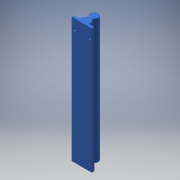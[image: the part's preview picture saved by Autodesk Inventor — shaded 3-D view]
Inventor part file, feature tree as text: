
AUTODESK INVENTOR PART (.ipt)
format: ipt  version: 2018 (Build 220112000, 112)  size: 141,824 bytes
history: native  units: mm
features: sketch x2, other x1, extrude x1, hole x1
ambient origin geometry x8: Origin, YZ Plane, XZ Plane, XY Plane, X Axis, Y Axis, Z Axis, Center Point
bodies: Body1 (feature_tree)
feature tree (5):
  other  "Sólido1"
  extrude  "Extrusão1"  Depth=25.0mm
  hole  "Furo1"  [1 undecoded]
  sketch  "Esboço1"  dims[d6=16.0mm d7=25.0mm]
  sketch  "Esboço3"  dims[d8=18.5mm d9=11.7mm d10=8.0mm d11=30.0deg d12=30.0deg d13=5.0mm d14=40.0mm d15=250.0mm d16=0.0mm d18=15.0mm d19=15.0mm d20=5.5mm d21=5.5mm d22=20.0mm d28=5.5mm d29=6.0mm d30=4.0mm d31=2.0mm d32=90.0deg d33=8.0mm d34=20.594885mm]
note: 1 required parameter value undecoded (feature->parameter linkage not recoverable at this tier; creation-order binding heuristic only, values carry confidence <= 0.55)
